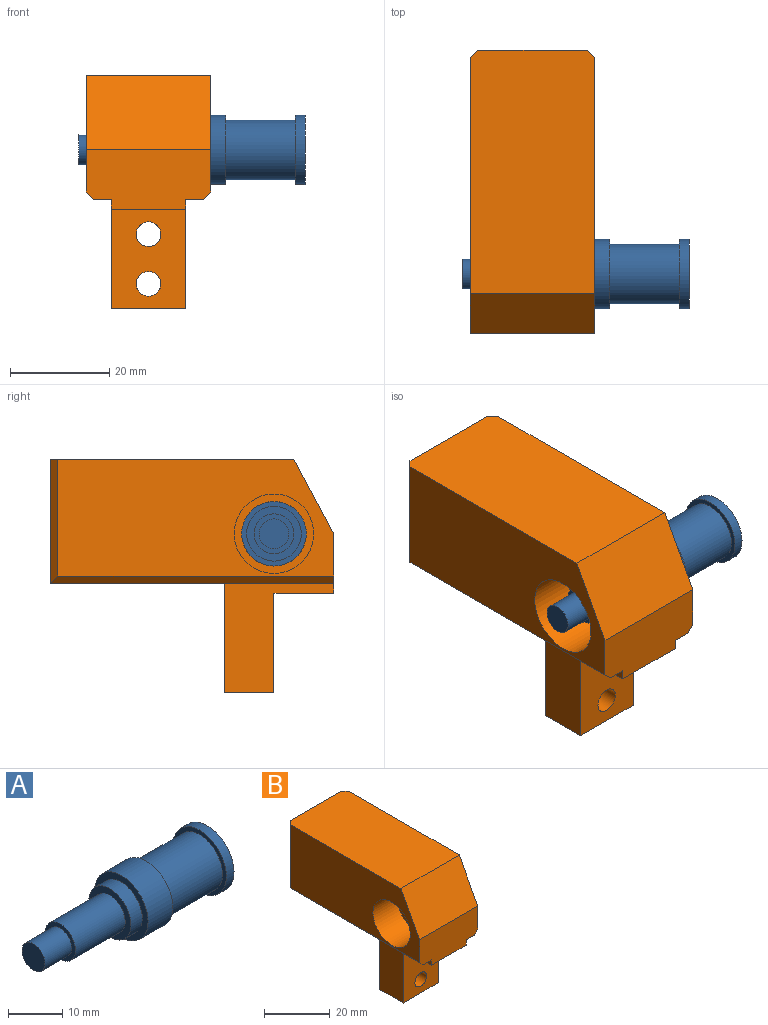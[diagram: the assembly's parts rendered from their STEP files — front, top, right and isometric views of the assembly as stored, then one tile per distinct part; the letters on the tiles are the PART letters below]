
ASSEMBLY  parts=2 mates=1
PART A: 13 faces, bbox 45.5x14x14 mm
  f0: plane 6x6mm, normal (-1,0,0), area 28.3mm2, adj f12
  f1: plane 14x14mm, normal (1,0,0), area 153.9mm2, adj f2
  f2: cylinder r=7mm len=14mm, axis (1,0,0), area 88mm2, adj f1,f3
  f3: plane 14x14mm, normal (-1,0,0), area 40.8mm2, adj f2,f4
  f4: cylinder r=6mm len=14mm, axis (1,0,0), area 527.8mm2, adj f3,f5
  f5: plane 14x14mm, normal (1,0,0), area 40.8mm2, adj f4,f6
  f6: cylinder r=7mm len=14mm, axis (1,0,0), area 285.9mm2, adj f5,f7
  f7: plane 14x14mm, normal (-1,0,0), area 58.9mm2, adj f6,f8
  f8: cylinder r=5.5mm len=11mm, axis (1,0,0), area 103.7mm2, adj f7,f9
  f9: plane 11x11mm, normal (-1,0,0), area 44.8mm2, adj f8,f10
  f10: cylinder r=4mm len=13mm, axis (1,0,0), area 326.7mm2, adj f9,f11
  f11: plane 8x8mm, normal (-1,0,0), area 22mm2, adj f10,f12
  f12: cylinder r=3mm len=7mm, axis (1,0,0), area 131.9mm2, adj f0,f11
PART B: 28 faces, bbox 25x57x47 mm
  f0: cylinder r=6.5mm len=13mm, axis (1,0,0), area 163.4mm2, adj f14,f16
  f1: plane 15x10mm, normal (0,0,-1), area 150mm2, adj f2,f3,f11,f13
  f2: plane 22x22mm, normal (-1,0,0), area 244mm2, adj f1,f5,f9,f11,f12,f13
  f3: plane 22x22mm, normal (1,0,0), area 244mm2, adj f1,f5,f9,f11,f12,f13
  f4: plane 55.5x23.5mm, normal (-1,0,0), area 1043.2mm2, adj f5,f8,f10,f17,f24,f25
  f5: plane 25x12mm, normal (0,-1,0), area 277.8mm2, adj f2,f3,f4,f7,f9,f10,f12,f25
  f6: plane 25x22mm, normal (0,1,0), area 550mm2, adj f8,f9,f24,f27
  f7: plane 55.5x23.5mm, normal (1,0,0), area 1043.2mm2, adj f5,f8,f10,f15,f26,f27
  f8: plane 49x25mm, normal (0,0,1), area 1222.7mm2, adj f4,f6,f7,f10,f24,f27
  f9: plane 57x22mm, normal (0,0,-1), area 924mm2, adj f2,f3,f5,f6,f13,f25,f26
  f10: plane 25x15mm, normal (0,-0.88,0.47), area 425mm2, adj f4,f5,f7,f8
  f11: plane 20x15mm, normal (0,-1,0), area 260.7mm2, adj f1,f2,f3,f12,f18,f21
  f12: plane 15x12mm, normal (0,0,-1), area 180mm2, adj f2,f3,f5,f11
  f13: plane 22x15mm, normal (0,1,0), area 202.8mm2, adj f1,f2,f3,f9,f20,f23
  f14: plane 16x16mm, normal (1,0,0), area 68.3mm2, adj f0,f15
  f15: cylinder r=8mm len=16mm, axis (1,0,0), area 527.8mm2, adj f7,f14
  f16: plane 16x16mm, normal (-1,0,0), area 68.3mm2, adj f0,f17
  f17: cylinder r=8mm len=16mm, axis (-1,0,0), area 527.8mm2, adj f4,f16
  f18: cylinder r=2.5mm len=5mm, axis (0,1,0), area 78.5mm2, adj f11,f19
  f19: plane 9x9mm, normal (0,1,0), area 44mm2, adj f18,f20
  f20: cylinder r=4.5mm len=9mm, axis (0,1,0), area 141.4mm2, adj f13,f19
  f21: cylinder r=2.5mm len=5mm, axis (0,1,0), area 78.5mm2, adj f11,f22
  f22: plane 9x9mm, normal (0,1,0), area 44mm2, adj f21,f23
  f23: cylinder r=4.5mm len=9mm, axis (0,1,0), area 141.4mm2, adj f13,f22
  f24: plane 25x1.5mm, normal (-0.71,0.71,0), area 51.4mm2, adj f4,f6,f8,f25
  f25: plane 57x1.5mm, normal (-0.71,0,-0.71), area 119.3mm2, adj f4,f5,f9,f24
  f26: plane 57x1.5mm, normal (0.71,0,-0.71), area 119.3mm2, adj f5,f7,f9,f27
  f27: plane 25x1.5mm, normal (0.71,0.71,0), area 51.4mm2, adj f6,f7,f8,f26
PLACE A t=(-38.1,-37.98,-2.85)mm
PLACE B t=(-24.1,7.02,-0.35)mm fixed
MATE revolute A.f2 <-> B.f15  axis (-1,0,0) through (-18.1,-37.98,-2.85)mm
